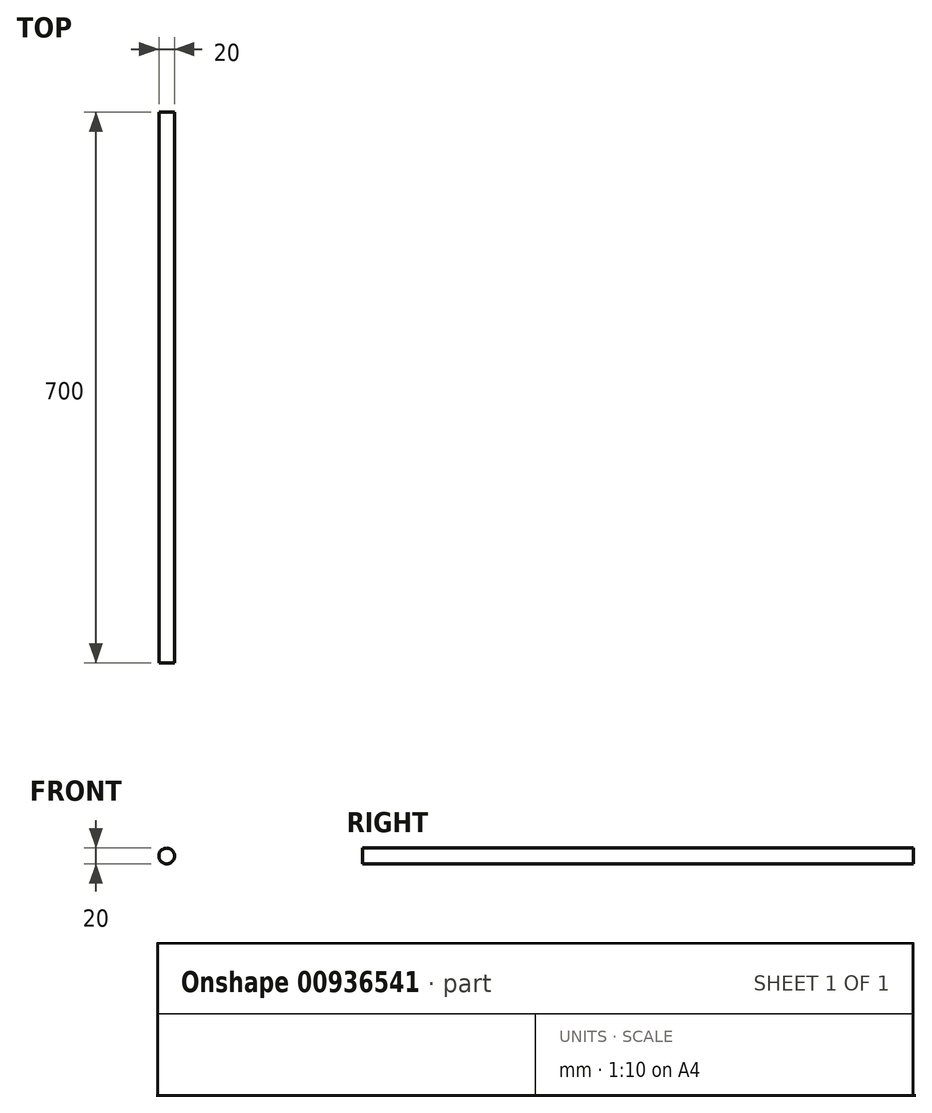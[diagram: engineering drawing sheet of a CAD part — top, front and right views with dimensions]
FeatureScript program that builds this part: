
annotation { "Feature Type Name" : "Feature", "Feature Type Description" : "" }
export const myFeature = defineFeature(function(context is Context, id is Id, definition is map)
    precondition{}
    {
        {
            var Q0;
            Q0=qCreatedBy(makeId("Front.planeOp"),FACE);
            var sketch = newSketch(context, id + "F0", { "sketchPlane" : qUnion([Q0])});
            skCircle(sketch, "E0", {"center": v(0, 0) * mm, "radius": 10 * mm});
            skSolve(sketch);
        }
        {
            var Q0;
            Q0=makeQuery(id+"F0.imprint","IMPRINT",FACE,{"disambiguationData":[TD([[makeQuery(id+"F0.imprint","IMPRINT",EDGE,{"derivedFrom":sQuery(id+"F0.wireOp",EDGE,"E0")}),1.0]])]});
            extrude(context, id + "F1", {"entities" : qUnion([Q0]), "depth" : 700 * mm, "offsetDistance" : 25.4 * mm});
        }
    });
